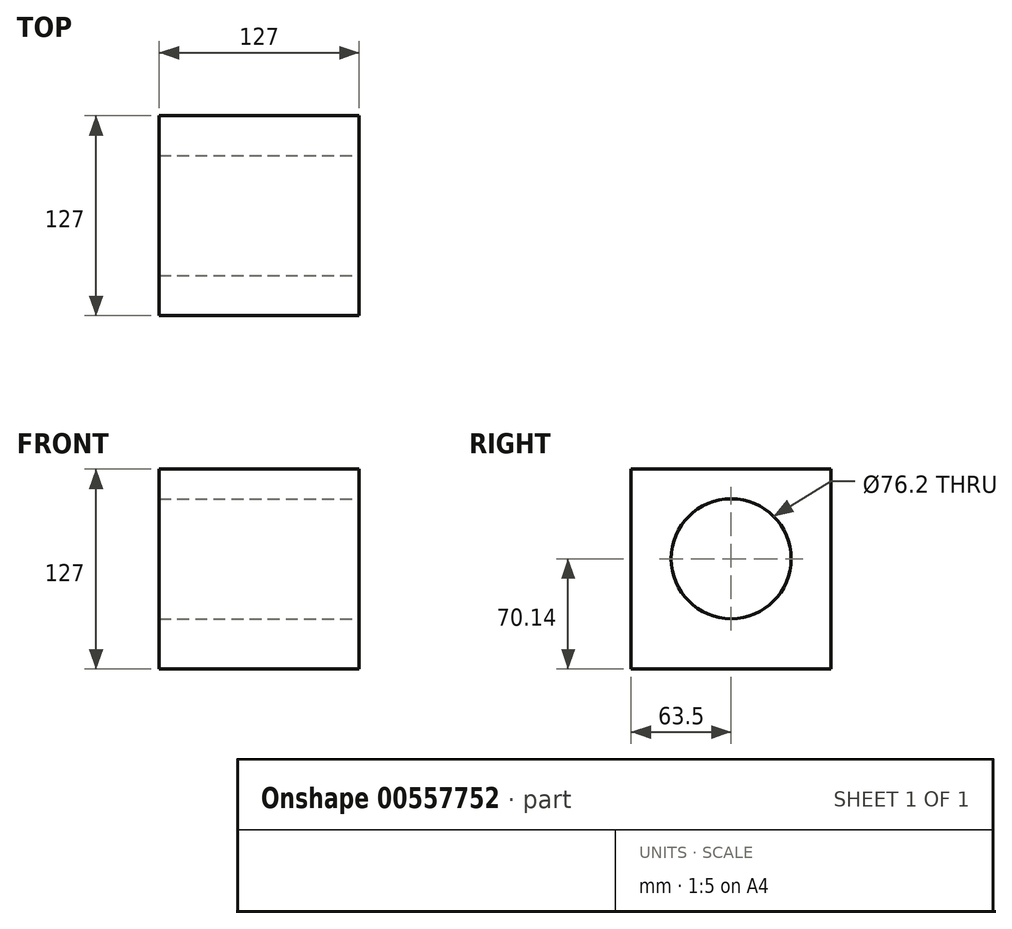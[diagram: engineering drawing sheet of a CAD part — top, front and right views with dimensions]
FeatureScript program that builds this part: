
annotation { "Feature Type Name" : "Feature", "Feature Type Description" : "" }
export const myFeature = defineFeature(function(context is Context, id is Id, definition is map)
    precondition{}
    {
        {
            var Q0;
            Q0=qCreatedBy(makeId("Front.planeOp"),FACE);
            var sketch = newSketch(context, id + "F0", { "sketchPlane" : qUnion([Q0])});
            skLineSegment(sketch, "E0", {"start": v(-55.91, 56.86) * mm, "end": v(71.09, 56.86) * mm});
            skLineSegment(sketch, "E1", {"start": v(71.09, 56.86) * mm, "end": v(71.09, -70.14) * mm});
            skLineSegment(sketch, "E2", {"start": v(71.09, -70.14) * mm, "end": v(-55.91, -70.14) * mm});
            skLineSegment(sketch, "E3", {"start": v(-55.91, -70.14) * mm, "end": v(-55.91, 56.86) * mm});
            skSolve(sketch);
        }
        {
            var Q0;
            Q0=makeQuery(id+"F0.imprint","IMPRINT",FACE,{"disambiguationData":[TD([[makeQuery(id+"F0.imprint","IMPRINT",EDGE,{"derivedFrom":sQuery(id+"F0.wireOp",EDGE,"E0")}),-1.0]])]});
            extrude(context, id + "F1", {"entities" : qUnion([Q0]), "oppositeDirection" : true, "depth" : 127 * mm, "offsetDistance" : 25.4 * mm});
        }
        {
            var Q0;
            Q0=makeQuery(id+"F1.opExtrude","SWEPT_FACE",FACE,{"disambiguationData":[OSD([sQuery(id+"F0.wireOp",EDGE,"E1")])]});
            var sketch = newSketch(context, id + "F2", { "sketchPlane" : qUnion([Q0])});
            skCircle(sketch, "E4", {"center": v(63.5, 0) * mm, "radius": 38.1 * mm});
            skPoint(sketch, "E4.centerSnap0", {"position": v(63.5, 56.86) * mm});
            skSolve(sketch);
        }
        {
            var Q0;
            Q0 = qSketchRegion(id + "F2", true);
            extrude(context, id + "F3", {"entities" : qUnion([Q0]), "operationType" : NewBodyOperationType.REMOVE, "endBound" : BoundingType.THROUGH_ALL, "oppositeDirection" : true, "depth" : 25.4 * mm, "offsetDistance" : 25.4 * mm});
        }
    });
